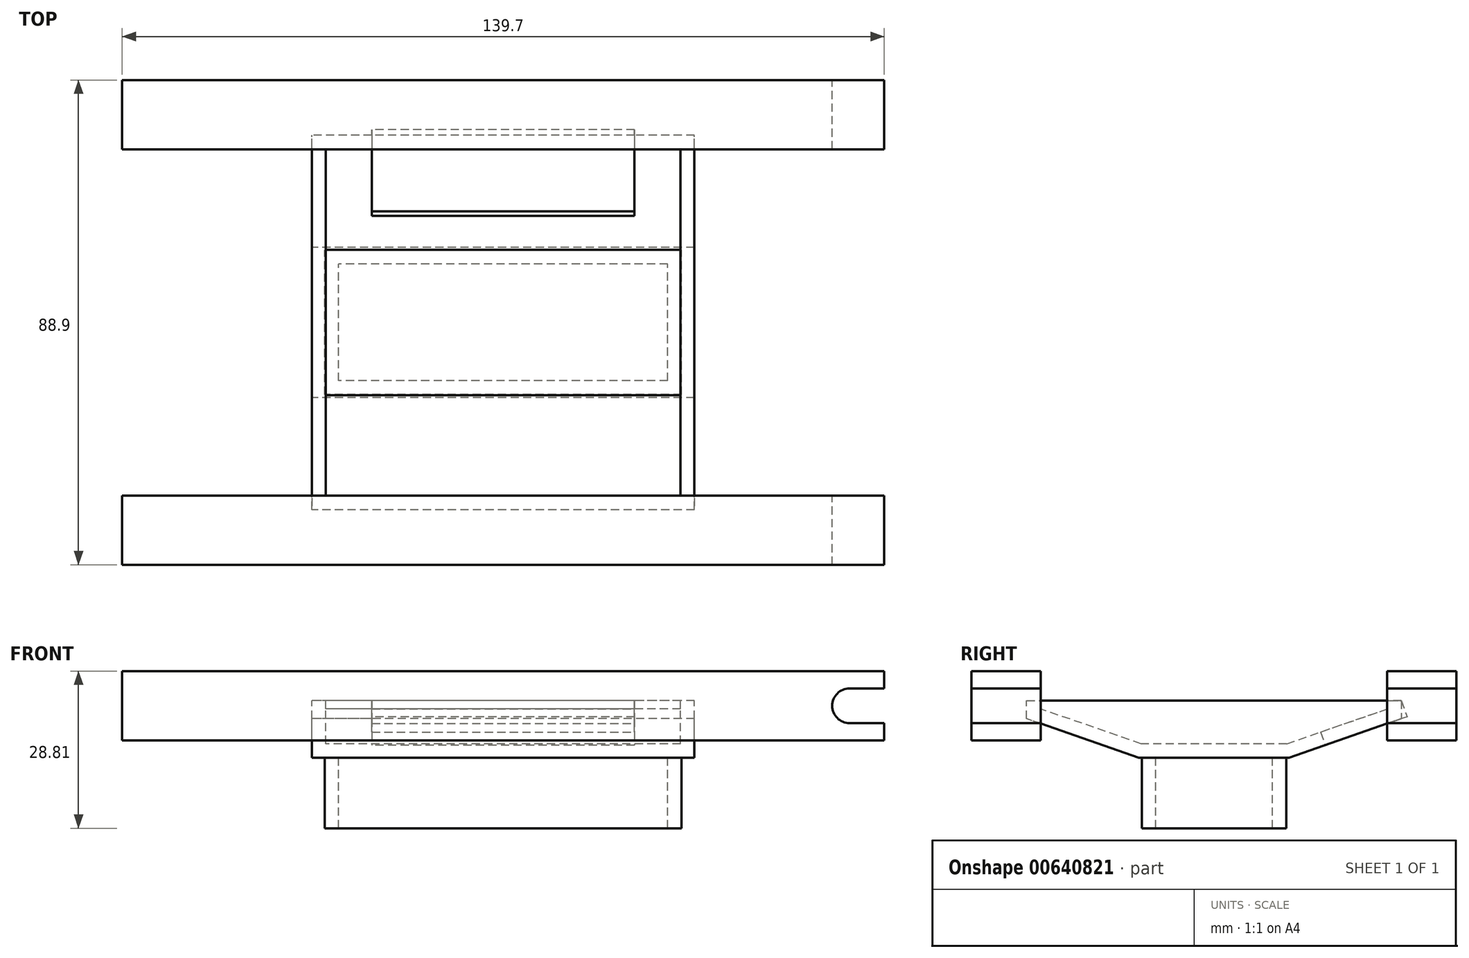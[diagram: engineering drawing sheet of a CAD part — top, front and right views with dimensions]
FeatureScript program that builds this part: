
annotation { "Feature Type Name" : "Feature", "Feature Type Description" : "" }
export const myFeature = defineFeature(function(context is Context, id is Id, definition is map)
    precondition{}
    {
        {
            var Q0;
            Q0=qCreatedBy(makeId("Right.planeOp"),FACE);
            var sketch = newSketch(context, id + "F0", { "sketchPlane" : qUnion([Q0])});
            skLineSegment(sketch, "E0.bottom", {"start": v(44.45, 3.16) * mm, "end": v(-44.45, 3.16) * mm});
            skLineSegment(sketch, "E0.top", {"start": v(44.45, 15.86) * mm, "end": v(-44.45, 15.86) * mm});
            skLineSegment(sketch, "E0.left", {"start": v(44.45, 3.16) * mm, "end": v(44.45, 15.86) * mm});
            skLineSegment(sketch, "E0.right", {"start": v(-44.45, 3.16) * mm, "end": v(-44.45, 15.86) * mm});
            skLineSegment(sketch, "E1", {"start": v(0, 3.16) * mm, "end": v(0, 15.86) * mm, "construction": true});
            skLineSegment(sketch, "E2", {"start": v(31.75, 3.16) * mm, "end": v(31.75, 15.86) * mm});
            skLineSegment(sketch, "E3", {"start": v(-31.75, 3.16) * mm, "end": v(-31.75, 15.86) * mm});
            skSolve(sketch);
        }
        {
            var Q0;
            {var subQ0=sQuery(id+"F0.wireOp",EDGE,"E0.left");Q0=makeQuery(id+"F0.imprint","IMPRINT",FACE,{"disambiguationData":[TD([[makeQuery(id+"F0.imprint","IMPRINT",EDGE,{"derivedFrom":subQ0}),1.0]])]});}
            var Q1;
            {var subQ0=sQuery(id+"F0.wireOp",EDGE,"E0.right");Q1=makeQuery(id+"F0.imprint","IMPRINT",FACE,{"disambiguationData":[TD([[makeQuery(id+"F0.imprint","IMPRINT",EDGE,{"derivedFrom":subQ0}),-1.0]])]});}
            extrude(context, id + "F1", {"entities" : qUnion([Q0, Q1]), "endBound" : BoundingType.SYMMETRIC, "depth" : 139.7 * mm, "offsetDistance" : 25.4 * mm});
        }
        {
            var Q0;
            Q0=qCreatedBy(makeId("Right.planeOp"),FACE);
            var sketch = newSketch(context, id + "F2", { "sketchPlane" : qUnion([Q0])});
            skLineSegment(sketch, "E4", {"start": v(0, 0) * mm, "end": v(-13.78, 0) * mm});
            skLineSegment(sketch, "E5", {"start": v(-13.78, 0) * mm, "end": v(-34.36, 7.14) * mm});
            skLineSegment(sketch, "E6", {"start": v(-34.36, 7.14) * mm, "end": v(-34.36, 10.46) * mm});
            skLineSegment(sketch, "E7", {"start": v(-34.36, 10.46) * mm, "end": v(0, 10.46) * mm});
            skLineSegment(sketch, "E8", {"start": v(0, 10.46) * mm, "end": v(0, 0) * mm});
            skSolve(sketch);
        }
        {
            var Q0;
            Q0=makeQuery(id+"F2.imprint","IMPRINT",FACE,{"disambiguationData":[TD([[makeQuery(id+"F2.imprint","IMPRINT",EDGE,{"derivedFrom":sQuery(id+"F2.wireOp",EDGE,"E4")}),-1.0]])]});
            extrude(context, id + "F3", {"entities" : qUnion([Q0]), "endBound" : BoundingType.SYMMETRIC, "depth" : 70.1 * mm, "offsetDistance" : 25.4 * mm});
        }
        {
            var Q0;
            Q0=makeQuery(id+"F3.opExtrude","SWEPT_BODY",BODY,{"disambiguationData":[OSD([sQuery(id+"F2.wireOp",EDGE,"E4"),sQuery(id+"F2.wireOp",EDGE,"E5"),sQuery(id+"F2.wireOp",EDGE,"E6"),sQuery(id+"F2.wireOp",EDGE,"E7"),sQuery(id+"F2.wireOp",EDGE,"E8")])]});
            var Q1;
            Q1=qCreatedBy(makeId("Front.planeOp"),FACE);
            mirror(context, id + "F4", {"entities" : qUnion([Q0]), "mirrorPlane" : qUnion([Q1])});
        }
        {
            var Q0;
            Q0=makeQuery(id+"F3.opExtrude","SWEPT_BODY",BODY,{"disambiguationData":[OSD([sQuery(id+"F2.wireOp",EDGE,"E4"),sQuery(id+"F2.wireOp",EDGE,"E5"),sQuery(id+"F2.wireOp",EDGE,"E6"),sQuery(id+"F2.wireOp",EDGE,"E7"),sQuery(id+"F2.wireOp",EDGE,"E8")])]});
            var Q1;
            Q1=makeQuery(id+"F4.opPattern","COPY",BODY,{"derivedFrom":makeQuery(id+"F3.opExtrude","SWEPT_BODY",BODY,{"disambiguationData":[OSD([sQuery(id+"F2.wireOp",EDGE,"E4"),sQuery(id+"F2.wireOp",EDGE,"E5"),sQuery(id+"F2.wireOp",EDGE,"E6"),sQuery(id+"F2.wireOp",EDGE,"E7"),sQuery(id+"F2.wireOp",EDGE,"E8")])]}),"instanceName":"1"});
            booleanBodies(context, id + "F5", {"operationType" : BooleanOperationType.UNION, "tools" : qUnion([Q0, Q1])});
        }
        {
            var Q0;
            {var subQ0=makeQuery(id+"F3.opExtrude","SWEPT_FACE",FACE,{"disambiguationData":[OSD([sQuery(id+"F2.wireOp",EDGE,"E4")])]});Q0=makeQuery(id+"F5.opBoolean","MERGE",FACE,{"derivedFrom":[subQ0,makeQuery(id+"F4.opPattern","COPY",FACE,{"derivedFrom":subQ0,"instanceName":"1"})]});}
            var sketch = newSketch(context, id + "F6", { "sketchPlane" : qUnion([Q0])});
            skLineSegment(sketch, "E9.bottom", {"start": v(30.16, 10.7) * mm, "end": v(-30.16, 10.7) * mm});
            skLineSegment(sketch, "E9.top", {"start": v(30.16, -10.7) * mm, "end": v(-30.16, -10.7) * mm});
            skLineSegment(sketch, "E9.left", {"start": v(30.16, 10.7) * mm, "end": v(30.16, -10.7) * mm});
            skLineSegment(sketch, "E9.right", {"start": v(-30.16, 10.7) * mm, "end": v(-30.16, -10.7) * mm});
            skPoint(sketch, "E9.middle", {"position": v(0, 0) * mm});
            skLineSegment(sketch, "E10.0", {"start": v(32.7, 13.25) * mm, "end": v(-32.7, 13.25) * mm});
            skLineSegment(sketch, "E10.1", {"start": v(32.7, 13.25) * mm, "end": v(32.7, -13.25) * mm});
            skLineSegment(sketch, "E10.2", {"start": v(32.7, -13.25) * mm, "end": v(-32.7, -13.25) * mm});
            skLineSegment(sketch, "E10.3", {"start": v(-32.7, 13.25) * mm, "end": v(-32.7, -13.25) * mm});
            skSolve(sketch);
        }
        {
            var Q0;
            Q0=makeQuery(id+"F6.imprint","IMPRINT",FACE,{"disambiguationData":[TD([[makeQuery(id+"F6.imprint","IMPRINT",EDGE,{"derivedFrom":sQuery(id+"F6.wireOp",EDGE,"E9.bottom")}),-1.0]])]});
            extrude(context, id + "F7", {"entities" : qUnion([Q0]), "operationType" : NewBodyOperationType.ADD, "depth" : 12.95 * mm, "offsetDistance" : 25.4 * mm});
        }
        {
            var Q0;
            {var subQ0=makeQuery(id+"F3.opExtrude","SWEPT_FACE",FACE,{"disambiguationData":[OSD([sQuery(id+"F2.wireOp",EDGE,"E7")])]});Q0=makeQuery(id+"F5.opBoolean","MERGE",FACE,{"derivedFrom":[subQ0,makeQuery(id+"F4.opPattern","COPY",FACE,{"derivedFrom":subQ0,"instanceName":"1"})]});}
            shell(context, id + "F8", {"entities" : qUnion([Q0]), "thickness" : 2.54 * mm});
        }
        {
            var Q0;
            Q0=makeQuery(id+"F4.opPattern","COPY",FACE,{"derivedFrom":makeQuery(id+"F3.opExtrude","SWEPT_FACE",FACE,{"disambiguationData":[OSD([sQuery(id+"F2.wireOp",EDGE,"E5")])]}),"instanceName":"1"});
            var sketch = newSketch(context, id + "F9", { "sketchPlane" : qUnion([Q0])});
            skLineSegment(sketch, "E11.bottom", {"start": v(24.08, -35.89) * mm, "end": v(-24.08, -35.89) * mm});
            skLineSegment(sketch, "E11.top", {"start": v(24.08, -19.99) * mm, "end": v(-24.08, -19.99) * mm});
            skLineSegment(sketch, "E11.left", {"start": v(24.08, -35.89) * mm, "end": v(24.08, -19.99) * mm});
            skLineSegment(sketch, "E11.right", {"start": v(-24.08, -35.89) * mm, "end": v(-24.08, -19.99) * mm});
            skPoint(sketch, "E11.middle", {"position": v(0, -27.94) * mm});
            skSolve(sketch);
        }
        {
            var Q0;
            {var subQ0=sQuery(id+"F9.wireOp",EDGE,"E11.top");Q0=makeQuery(id+"F9.imprint","IMPRINT",FACE,{"disambiguationData":[TD([[makeQuery(id+"F9.imprint","IMPRINT",EDGE,{"derivedFrom":subQ0}),1.0]])]});}
            var Q1;
            {var subQ0=sQuery(id+"F9.wireOp",EDGE,"E11.bottom");Q1=makeQuery(id+"F9.imprint","IMPRINT",FACE,{"disambiguationData":[TD([[makeQuery(id+"F9.imprint","IMPRINT",EDGE,{"derivedFrom":subQ0}),-1.0]])]});}
            extrude(context, id + "F10", {"entities" : qUnion([Q0, Q1]), "operationType" : NewBodyOperationType.REMOVE, "endBound" : BoundingType.UP_TO_NEXT, "oppositeDirection" : true, "depth" : 25.4 * mm, "offsetDistance" : 25.4 * mm});
        }
        {
            var Q0;
            Q0=makeQuery(id+"F1.opExtrude","SWEPT_FACE",FACE,{"disambiguationData":[OSD([sQuery(id+"F0.wireOp",EDGE,"E0.left")])]});
            var sketch = newSketch(context, id + "F11", { "sketchPlane" : qUnion([Q0])});
            skLineSegment(sketch, "E12", {"start": v(-69.85, 9.5) * mm, "end": v(-63.5, 9.5) * mm, "construction": true});
            skArc(sketch, "E13", {"start": v(-63.5, 6.33) * mm, "mid": v(-60.33, 9.5) * mm, "end": v(-63.5, 12.68) * mm});
            skLineSegment(sketch, "E14", {"start": v(-63.5, 9.5) * mm, "end": v(-63.5, 12.68) * mm, "construction": true});
            skLineSegment(sketch, "E15", {"start": v(-63.5, 12.68) * mm, "end": v(-69.85, 12.68) * mm});
            skLineSegment(sketch, "E16", {"start": v(-63.5, 9.5) * mm, "end": v(-63.5, 6.33) * mm, "construction": true});
            skLineSegment(sketch, "E17", {"start": v(-63.5, 6.33) * mm, "end": v(-69.85, 6.33) * mm});
            skLineSegment(sketch, "E18", {"start": v(-69.85, 12.68) * mm, "end": v(-69.85, 6.33) * mm});
            skSolve(sketch);
        }
        {
            var Q0;
            Q0=makeQuery(id+"F11.imprint","IMPRINT",FACE,{"disambiguationData":[TD([[makeQuery(id+"F11.imprint","IMPRINT",EDGE,{"derivedFrom":sQuery(id+"F11.wireOp",EDGE,"E13")}),1.0]])]});
            extrude(context, id + "F12", {"entities" : qUnion([Q0]), "operationType" : NewBodyOperationType.REMOVE, "endBound" : BoundingType.THROUGH_ALL, "oppositeDirection" : true, "depth" : 25.4 * mm, "offsetDistance" : 25.4 * mm});
        }
    });
